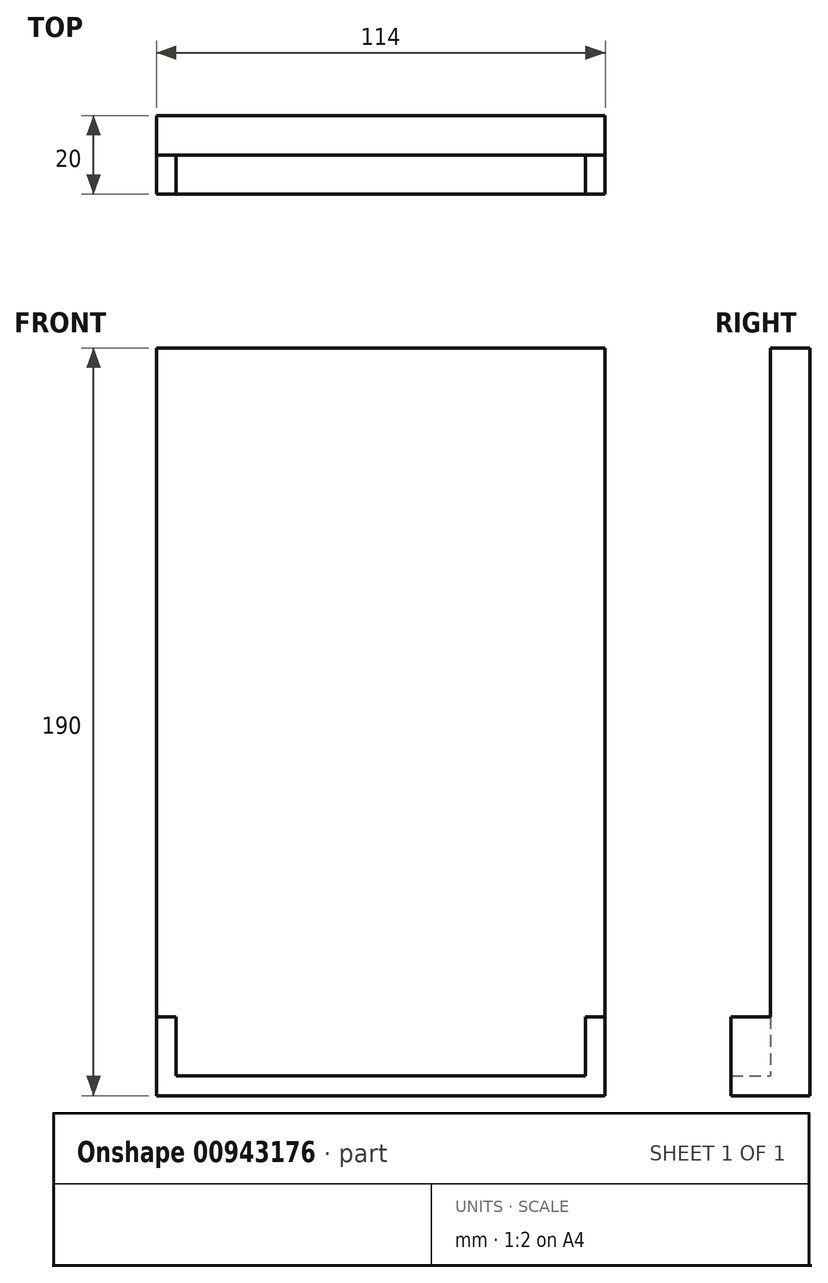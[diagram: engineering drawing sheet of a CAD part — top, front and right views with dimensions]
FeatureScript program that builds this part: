
annotation { "Feature Type Name" : "Feature", "Feature Type Description" : "" }
export const myFeature = defineFeature(function(context is Context, id is Id, definition is map)
    precondition{}
    {
        {
            var Q0;
            Q0=qCreatedBy(makeId("Front.planeOp"),FACE);
            var sketch = newSketch(context, id + "F0", { "sketchPlane" : qUnion([Q0])});
            skLineSegment(sketch, "E0.bottom", {"start": v(-56.5, 99.55) * mm, "end": v(57.5, 99.55) * mm});
            skLineSegment(sketch, "E0.top", {"start": v(-56.5, -90.45) * mm, "end": v(57.5, -90.45) * mm});
            skLineSegment(sketch, "E0.left", {"start": v(-56.5, 99.55) * mm, "end": v(-56.5, -90.45) * mm});
            skLineSegment(sketch, "E0.right", {"start": v(57.5, 99.55) * mm, "end": v(57.5, -90.45) * mm});
            skLineSegment(sketch, "E1", {"start": v(-56.5, -85.45) * mm, "end": v(57.5, -85.45) * mm});
            skLineSegment(sketch, "E2", {"start": v(-56.5, -70.45) * mm, "end": v(57.5, -70.45) * mm});
            skLineSegment(sketch, "E3", {"start": v(52.5, -70.45) * mm, "end": v(52.5, -90.45) * mm});
            skLineSegment(sketch, "E4", {"start": v(-51.5, -70.45) * mm, "end": v(-51.5, -90.45) * mm});
            skSolve(sketch);
        }
        {
            var Q0;
            {var subQ0=sQuery(id+"F0.wireOp",EDGE,"E3");var subQ1=sQuery(id+"F0.wireOp",EDGE,"E0.top");var subQ2=makeQuery(id+"F0.imprint","INTERSECT",VERTEX,{"derivedFrom":[subQ1,subQ0]});Q0=makeQuery(id+"F0.imprint","IMPRINT",FACE,{"disambiguationData":[TD([[makeQuery(id+"F0.imprint","IMPRINT",EDGE,{"disambiguationData":[TD([[subQ2,1.0]])],"derivedFrom":subQ1}),1.0]])]});}
            var Q1;
            {var subQ0=sQuery(id+"F0.wireOp",EDGE,"E0.left");var subQ1=sQuery(id+"F0.wireOp",EDGE,"E0.top");var subQ2=makeQuery(id+"F0.imprint","INTERSECT",VERTEX,{"derivedFrom":[subQ1,subQ0]});Q1=makeQuery(id+"F0.imprint","IMPRINT",FACE,{"disambiguationData":[TD([[makeQuery(id+"F0.imprint","IMPRINT",EDGE,{"disambiguationData":[TD([[subQ2,-1.0]])],"derivedFrom":subQ1}),1.0]])]});}
            var Q2;
            {var subQ0=sQuery(id+"F0.wireOp",EDGE,"E1");var subQ1=sQuery(id+"F0.wireOp",EDGE,"E0.left");var subQ2=makeQuery(id+"F0.imprint","INTERSECT",VERTEX,{"derivedFrom":[subQ1,subQ0]});Q2=makeQuery(id+"F0.imprint","IMPRINT",FACE,{"disambiguationData":[TD([[makeQuery(id+"F0.imprint","IMPRINT",EDGE,{"disambiguationData":[TD([[subQ2,1.0]])],"derivedFrom":subQ1}),1.0]])]});}
            var Q3;
            {var subQ0=sQuery(id+"F0.wireOp",EDGE,"E1");var subQ1=sQuery(id+"F0.wireOp",EDGE,"E0.right");var subQ2=makeQuery(id+"F0.imprint","INTERSECT",VERTEX,{"derivedFrom":[subQ1,subQ0]});Q3=makeQuery(id+"F0.imprint","IMPRINT",FACE,{"disambiguationData":[TD([[makeQuery(id+"F0.imprint","IMPRINT",EDGE,{"disambiguationData":[TD([[subQ2,1.0]])],"derivedFrom":subQ1}),-1.0]])]});}
            var Q4;
            {var subQ0=sQuery(id+"F0.wireOp",EDGE,"E0.right");var subQ1=sQuery(id+"F0.wireOp",EDGE,"E0.top");var subQ2=makeQuery(id+"F0.imprint","INTERSECT",VERTEX,{"derivedFrom":[subQ1,subQ0]});Q4=makeQuery(id+"F0.imprint","IMPRINT",FACE,{"disambiguationData":[TD([[makeQuery(id+"F0.imprint","IMPRINT",EDGE,{"disambiguationData":[TD([[subQ2,1.0]])],"derivedFrom":subQ1}),1.0]])]});}
            extrude(context, id + "F1", {"entities" : qUnion([Q0, Q1, Q2, Q3, Q4]), "depth" : 10 * mm, "offsetDistance" : 25.4 * mm});
        }
        {
            var Q0;
            {var subQ0=sQuery(id+"F0.wireOp",EDGE,"E0.left");var subQ1=sQuery(id+"F0.wireOp",EDGE,"E0.top");var subQ2=makeQuery(id+"F0.imprint","INTERSECT",VERTEX,{"derivedFrom":[subQ1,subQ0]});Q0=makeQuery(id+"F0.imprint","IMPRINT",FACE,{"disambiguationData":[TD([[makeQuery(id+"F0.imprint","IMPRINT",EDGE,{"disambiguationData":[TD([[subQ2,-1.0]])],"derivedFrom":subQ1}),1.0]])]});}
            var Q1;
            {var subQ0=sQuery(id+"F0.wireOp",EDGE,"E0.right");var subQ1=sQuery(id+"F0.wireOp",EDGE,"E0.top");var subQ2=makeQuery(id+"F0.imprint","INTERSECT",VERTEX,{"derivedFrom":[subQ1,subQ0]});Q1=makeQuery(id+"F0.imprint","IMPRINT",FACE,{"disambiguationData":[TD([[makeQuery(id+"F0.imprint","IMPRINT",EDGE,{"disambiguationData":[TD([[subQ2,1.0]])],"derivedFrom":subQ1}),1.0]])]});}
            var Q2;
            {var subQ0=sQuery(id+"F0.wireOp",EDGE,"E3");var subQ1=sQuery(id+"F0.wireOp",EDGE,"E0.top");var subQ2=makeQuery(id+"F0.imprint","INTERSECT",VERTEX,{"derivedFrom":[subQ1,subQ0]});Q2=makeQuery(id+"F0.imprint","IMPRINT",FACE,{"disambiguationData":[TD([[makeQuery(id+"F0.imprint","IMPRINT",EDGE,{"disambiguationData":[TD([[subQ2,1.0]])],"derivedFrom":subQ1}),1.0]])]});}
            var Q3;
            {var subQ0=sQuery(id+"F0.wireOp",EDGE,"E1");var subQ1=sQuery(id+"F0.wireOp",EDGE,"E0.left");var subQ2=makeQuery(id+"F0.imprint","INTERSECT",VERTEX,{"derivedFrom":[subQ1,subQ0]});Q3=makeQuery(id+"F0.imprint","IMPRINT",FACE,{"disambiguationData":[TD([[makeQuery(id+"F0.imprint","IMPRINT",EDGE,{"disambiguationData":[TD([[subQ2,1.0]])],"derivedFrom":subQ1}),1.0]])]});}
            var Q4;
            {var subQ0=sQuery(id+"F0.wireOp",EDGE,"E1");var subQ1=sQuery(id+"F0.wireOp",EDGE,"E0.right");var subQ2=makeQuery(id+"F0.imprint","INTERSECT",VERTEX,{"derivedFrom":[subQ1,subQ0]});Q4=makeQuery(id+"F0.imprint","IMPRINT",FACE,{"disambiguationData":[TD([[makeQuery(id+"F0.imprint","IMPRINT",EDGE,{"disambiguationData":[TD([[subQ2,1.0]])],"derivedFrom":subQ1}),-1.0]])]});}
            var Q5;
            {var subQ0=sQuery(id+"F0.wireOp",EDGE,"E4");var subQ1=sQuery(id+"F0.wireOp",EDGE,"E1");var subQ2=makeQuery(id+"F0.imprint","INTERSECT",VERTEX,{"derivedFrom":[subQ1,subQ0]});Q5=makeQuery(id+"F0.imprint","IMPRINT",FACE,{"disambiguationData":[TD([[makeQuery(id+"F0.imprint","IMPRINT",EDGE,{"disambiguationData":[TD([[subQ2,-1.0]])],"derivedFrom":subQ1}),1.0]])]});}
            var Q6;
            {var subQ5=sQuery(id+"F0.wireOp",EDGE,"E0.bottom");Q6=makeQuery(id+"F0.imprint","IMPRINT",FACE,{"disambiguationData":[TD([[makeQuery(id+"F0.imprint","IMPRINT",EDGE,{"derivedFrom":subQ5}),-1.0]])]});}
            extrude(context, id + "F2", {"entities" : qUnion([Q0, Q1, Q2, Q3, Q4, Q5, Q6]), "operationType" : NewBodyOperationType.ADD, "depth" : -10 * mm, "offsetDistance" : 25.4 * mm});
        }
    });
